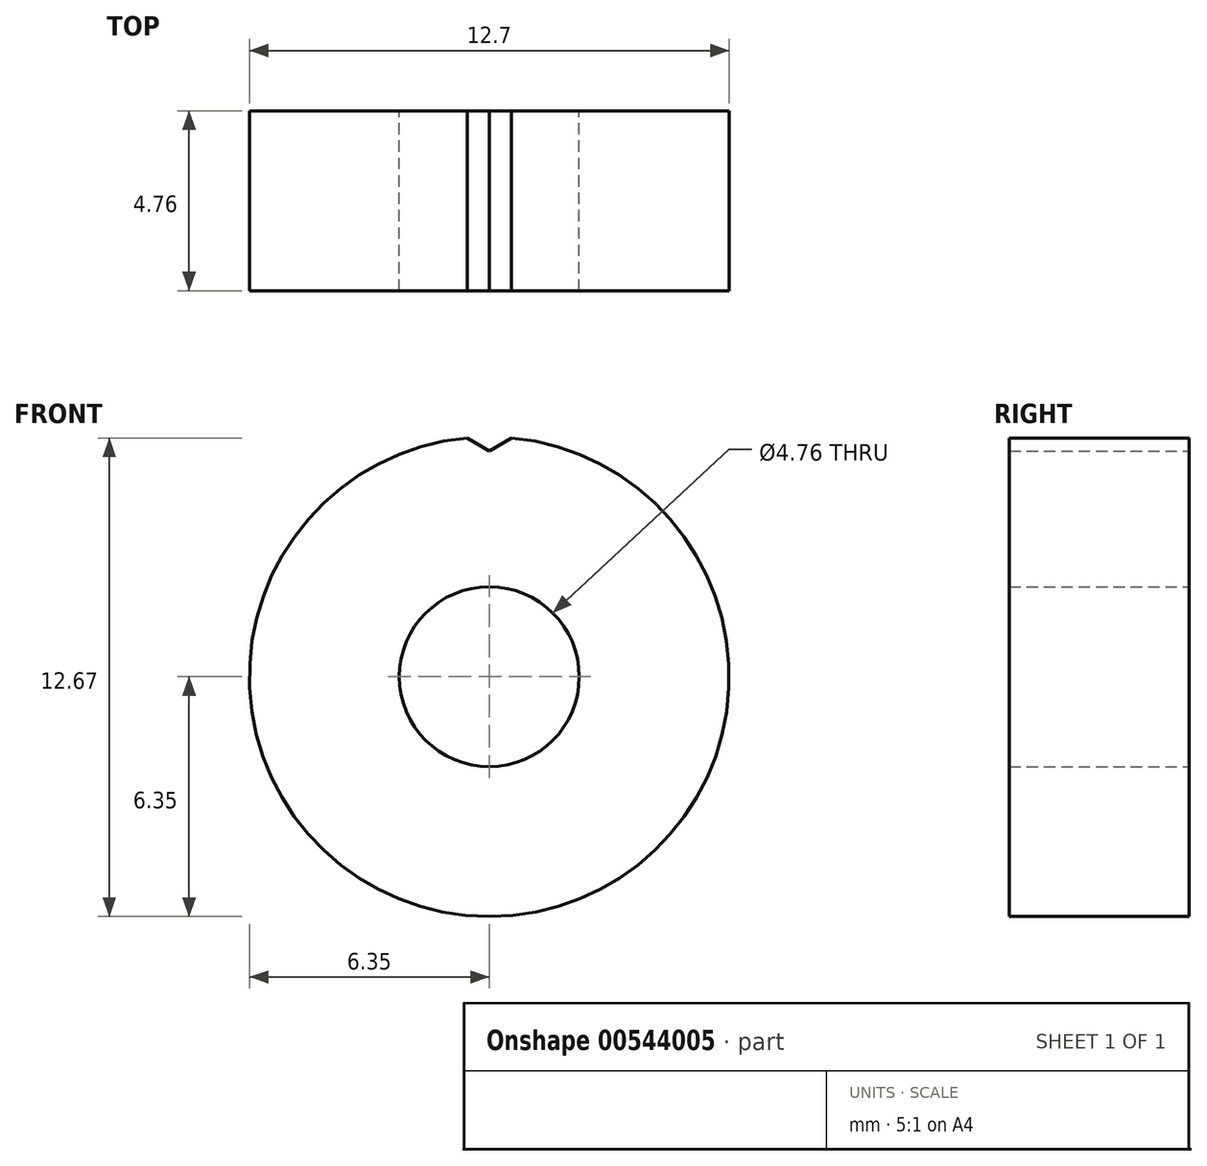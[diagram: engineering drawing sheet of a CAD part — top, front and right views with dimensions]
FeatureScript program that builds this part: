
annotation { "Feature Type Name" : "Feature", "Feature Type Description" : "" }
export const myFeature = defineFeature(function(context is Context, id is Id, definition is map)
    precondition{}
    {
        {
            var Q0;
            Q0=qCreatedBy(makeId("Front.planeOp"),FACE);
            var sketch = newSketch(context, id + "F0", { "sketchPlane" : qUnion([Q0])});
            skCircle(sketch, "E0", {"center": v(0, 0) * mm, "radius": 2.38 * mm});
            skCircle(sketch, "E1", {"center": v(0, 0) * mm, "radius": 6.35 * mm});
            skSolve(sketch);
        }
        {
            var Q0;
            Q0 = qSketchRegion(id + "F0", true);
            extrude(context, id + "F1", {"entities" : qUnion([Q0]), "depth" : 4.76 * mm, "offsetDistance" : 25.4 * mm});
        }
        {
            var Q0;
            Q0=qCreatedBy(makeId("Front.planeOp"),FACE);
            var sketch = newSketch(context, id + "F2", { "sketchPlane" : qUnion([Q0])});
            skCircle(sketch, "E2", {"center": v(0, 0) * mm, "radius": 5.97 * mm, "construction": true});
            skLineSegment(sketch, "E3", {"start": v(0, 6.35) * mm, "end": v(0, 0) * mm, "construction": true});
            skLineSegment(sketch, "E4", {"start": v(0, 0) * mm, "end": v(0.59, 6.32) * mm, "construction": true});
            skLineSegment(sketch, "E5", {"start": v(0, 5.97) * mm, "end": v(0.59, 6.32) * mm});
            skLineSegment(sketch, "E6", {"start": v(0, 5.97) * mm, "end": v(-0.59, 6.32) * mm});
            skArc(sketch, "E7", {"start": v(0.59, 6.32) * mm, "mid": v(0, 6.47) * mm, "end": v(-0.59, 6.32) * mm});
            skSolve(sketch);
        }
        {
            var Q0;
            Q0 = qSketchRegion(id + "F2", true);
            extrude(context, id + "F3", {"entities" : qUnion([Q0]), "operationType" : NewBodyOperationType.REMOVE, "endBound" : BoundingType.THROUGH_ALL, "depth" : 25.4 * mm, "offsetDistance" : 25.4 * mm});
        }
    });
